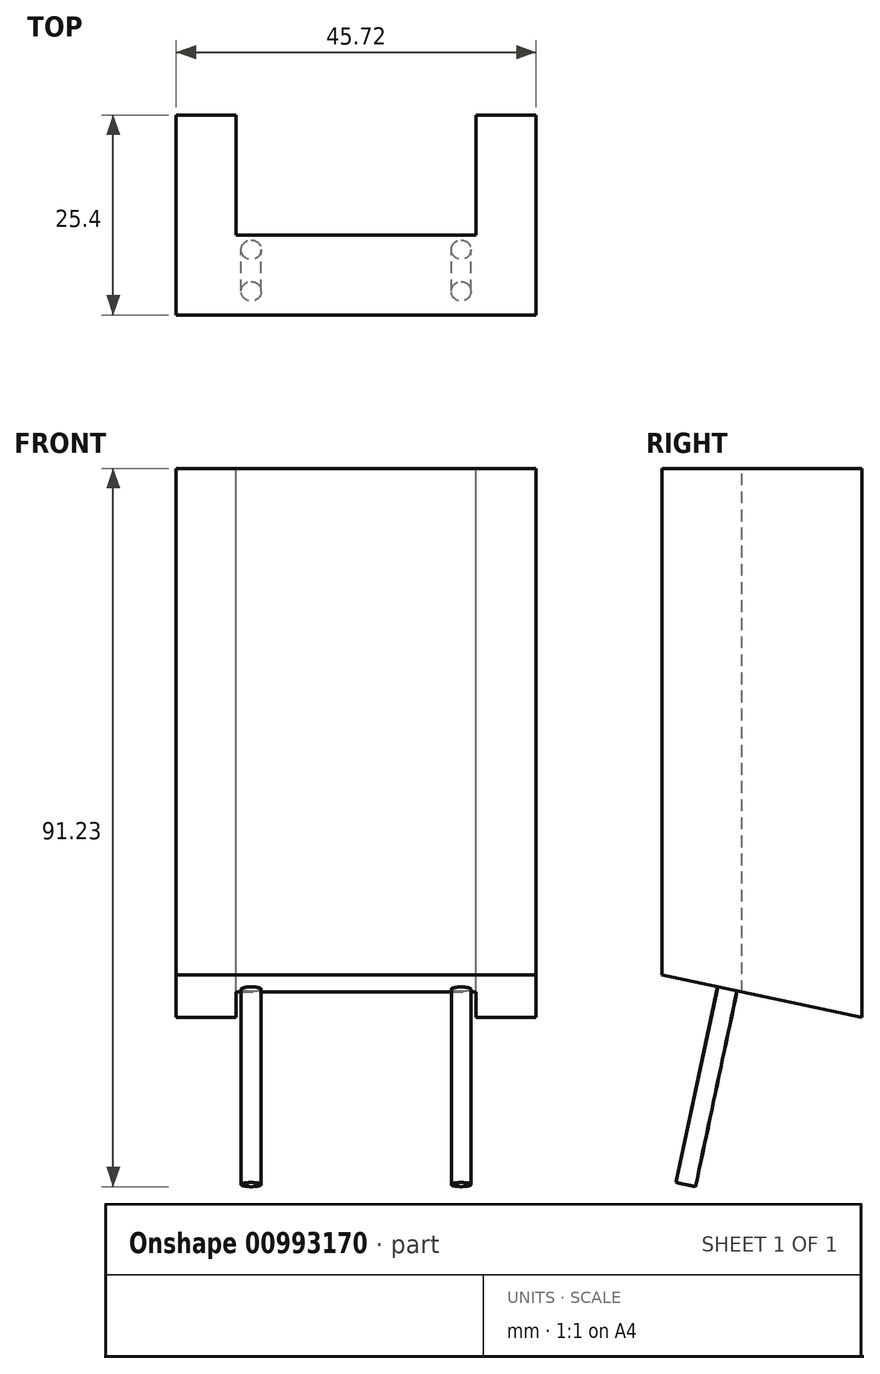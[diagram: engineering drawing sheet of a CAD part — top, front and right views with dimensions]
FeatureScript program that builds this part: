
annotation { "Feature Type Name" : "Feature", "Feature Type Description" : "" }
export const myFeature = defineFeature(function(context is Context, id is Id, definition is map)
    precondition{}
    {
        {
            var Q0;
            Q0=qCreatedBy(makeId("Right.planeOp"),FACE);
            var sketch = newSketch(context, id + "F0", { "sketchPlane" : qUnion([Q0])});
            skLineSegment(sketch, "E0.bottom", {"start": v(-45.3, 49.1) * mm, "end": v(-19.9, 49.1) * mm});
            skLineSegment(sketch, "E0.top", {"start": v(-45.3, -20.65) * mm, "end": v(-19.9, -20.65) * mm});
            skLineSegment(sketch, "E0.left", {"start": v(-45.3, 49.1) * mm, "end": v(-45.3, -20.65) * mm});
            skLineSegment(sketch, "E0.right", {"start": v(-19.9, 49.1) * mm, "end": v(-19.9, -20.65) * mm});
            skLineSegment(sketch, "E1", {"start": v(-19.9, -20.65) * mm, "end": v(-49.72, -14.32) * mm});
            skLineSegment(sketch, "E2", {"start": v(-37.68, -16.88) * mm, "end": v(-37.68, 49.1) * mm});
            skLineSegment(sketch, "E3", {"start": v(-49.72, 49.1) * mm, "end": v(-45.3, 49.1) * mm});
            skLineSegment(sketch, "E4", {"start": v(-49.72, -14.32) * mm, "end": v(-49.72, 49.1) * mm});
            skSolve(sketch);
        }
        {
            var Q0;
            {var subQ0=sQuery(id+"F0.wireOp",EDGE,"E0.right");Q0=makeQuery(id+"F0.imprint","IMPRINT",FACE,{"disambiguationData":[TD([[makeQuery(id+"F0.imprint","IMPRINT",EDGE,{"derivedFrom":subQ0}),-1.0]])]});}
            var Q1;
            {var subQ9=sQuery(id+"F0.wireOp",EDGE,"E2");Q1=makeQuery(id+"F0.imprint","IMPRINT",FACE,{"disambiguationData":[TD([[makeQuery(id+"F0.imprint","IMPRINT",EDGE,{"derivedFrom":subQ9}),1.0]])]});}
            var Q2;
            {var subQ0=sQuery(id+"F0.wireOp",EDGE,"v3j3xiSU-bfe7-Lb3w-s0aW-wV5Ot5F78tt4");var subQ1=sQuery(id+"F0.wireOp",EDGE,"E0.left");var subQ2=makeQuery(id+"F0.imprint","INTERSECT",VERTEX,{"derivedFrom":[subQ1,subQ0]});Q2=makeQuery(id+"F0.imprint","IMPRINT",FACE,{"disambiguationData":[TD([[makeQuery(id+"F0.imprint","IMPRINT",EDGE,{"disambiguationData":[TD([[subQ2,-1.0]])],"derivedFrom":subQ1}),-1.0]])]});}
            var Q3;
            {var subQ0=sQuery(id+"F0.wireOp",EDGE,"T0aaNbOe-sIyb-AqDr-S19V-MmI8U7dZupkg");Q3=makeQuery(id+"F0.imprint","IMPRINT",FACE,{"disambiguationData":[TD([[makeQuery(id+"F0.imprint","IMPRINT",EDGE,{"derivedFrom":subQ0}),1.0]])]});}
            var Q4;
            {var subQ0=sQuery(id+"F0.wireOp",EDGE,"vjtYr1df-9ol8-CtkE-OAvC-cVhov4n5x2EU");Q4=makeQuery(id+"F0.imprint","IMPRINT",FACE,{"disambiguationData":[TD([[makeQuery(id+"F0.imprint","IMPRINT",EDGE,{"derivedFrom":subQ0}),-1.0]])]});}
            extrude(context, id + "F1", {"entities" : qUnion([Q0, Q1, Q2, Q3, Q4]), "depth" : 7.62 * mm, "offsetDistance" : 25.4 * mm, "hasSecondDirection" : true, "secondDirectionOppositeDirection" : true, "secondDirectionDepth" : 38.1 * mm});
        }
        {
            var Q0;
            {var subQ0=sQuery(id+"F0.wireOp",EDGE,"T0aaNbOe-sIyb-AqDr-S19V-MmI8U7dZupkg");Q0=makeQuery(id+"F0.imprint","IMPRINT",FACE,{"disambiguationData":[TD([[makeQuery(id+"F0.imprint","IMPRINT",EDGE,{"derivedFrom":subQ0}),1.0]])]});}
            var Q1;
            {var subQ9=sQuery(id+"F0.wireOp",EDGE,"E2");Q1=makeQuery(id+"F0.imprint","IMPRINT",FACE,{"disambiguationData":[TD([[makeQuery(id+"F0.imprint","IMPRINT",EDGE,{"derivedFrom":subQ9}),1.0]])]});}
            var Q2;
            {var subQ0=sQuery(id+"F0.wireOp",EDGE,"v3j3xiSU-bfe7-Lb3w-s0aW-wV5Ot5F78tt4");var subQ1=sQuery(id+"F0.wireOp",EDGE,"E0.left");var subQ2=makeQuery(id+"F0.imprint","INTERSECT",VERTEX,{"derivedFrom":[subQ1,subQ0]});Q2=makeQuery(id+"F0.imprint","IMPRINT",FACE,{"disambiguationData":[TD([[makeQuery(id+"F0.imprint","IMPRINT",EDGE,{"disambiguationData":[TD([[subQ2,-1.0]])],"derivedFrom":subQ1}),-1.0]])]});}
            extrude(context, id + "F2", {"entities" : qUnion([Q0, Q1, Q2]), "operationType" : NewBodyOperationType.ADD, "oppositeDirection" : true, "depth" : 15.24 * mm, "offsetDistance" : 25.4 * mm});
        }
        {
            var Q0;
            Q0=makeQuery(id+"F1.opExtrude","SWEPT_FACE",FACE,{"disambiguationData":[OSD([sQuery(id+"F0.wireOp",EDGE,"E0.bottom"),sQuery(id+"F0.wireOp",EDGE,"T0aaNbOe-sIyb-AqDr-S19V-MmI8U7dZupkg")])]});
            var sketch = newSketch(context, id + "F3", { "sketchPlane" : qUnion([Q0])});
            skLineSegment(sketch, "E5.bottom", {"start": v(0, -19.9) * mm, "end": v(-30.48, -19.9) * mm});
            skLineSegment(sketch, "E5.top", {"start": v(0, -35.14) * mm, "end": v(-30.48, -35.14) * mm});
            skLineSegment(sketch, "E5.left", {"start": v(0, -19.9) * mm, "end": v(0, -35.14) * mm});
            skLineSegment(sketch, "E5.right", {"start": v(-30.48, -19.9) * mm, "end": v(-30.48, -35.14) * mm});
            skPoint(sketch, "E5.middle", {"position": v(-15.24, -27.52) * mm});
            skPoint(sketch, "E5.middle.positionSnap0", {"position": v(-15.24, -19.9) * mm});
            skPoint(sketch, "E5.centerSnap0", {"position": v(-15.24, -19.9) * mm});
            skSolve(sketch);
        }
        {
            var Q0;
            Q0=makeQuery(id+"F3.imprint","IMPRINT",FACE,{"disambiguationData":[TD([[makeQuery(id+"F3.imprint","IMPRINT",EDGE,{"derivedFrom":sQuery(id+"F3.wireOp",EDGE,"E5.bottom")}),1.0]])]});
            extrude(context, id + "F4", {"entities" : qUnion([Q0]), "operationType" : NewBodyOperationType.REMOVE, "oppositeDirection" : true, "depth" : 152.4 * mm, "offsetDistance" : 25.4 * mm});
        }
        {
            var Q0;
            Q0=makeQuery(id+"F1.opExtrude","SWEPT_FACE",FACE,{"disambiguationData":[OSD([sQuery(id+"F0.wireOp",EDGE,"E1")])]});
            var sketch = newSketch(context, id + "F5", { "sketchPlane" : qUnion([Q0])});
            skCircle(sketch, "E6", {"center": v(-28.58, 32.66) * mm, "radius": 1.27 * mm});
            skCircle(sketch, "E7", {"center": v(-1.9, 32.66) * mm, "radius": 1.25 * mm});
            skSolve(sketch);
        }
        {
            var Q0;
            Q0=makeQuery(id+"F5.imprint","IMPRINT",FACE,{"disambiguationData":[TD([[makeQuery(id+"F5.imprint","IMPRINT",EDGE,{"derivedFrom":sQuery(id+"F5.wireOp",EDGE,"E6")}),1.0]])]});
            var Q1;
            Q1=makeQuery(id+"F5.imprint","IMPRINT",FACE,{"disambiguationData":[TD([[makeQuery(id+"F5.imprint","IMPRINT",EDGE,{"derivedFrom":sQuery(id+"F5.wireOp",EDGE,"E7")}),1.0]])]});
            extrude(context, id + "F6", {"entities" : qUnion([Q0, Q1]), "operationType" : NewBodyOperationType.ADD, "depth" : 25.4 * mm, "offsetDistance" : 25.4 * mm});
        }
    });
